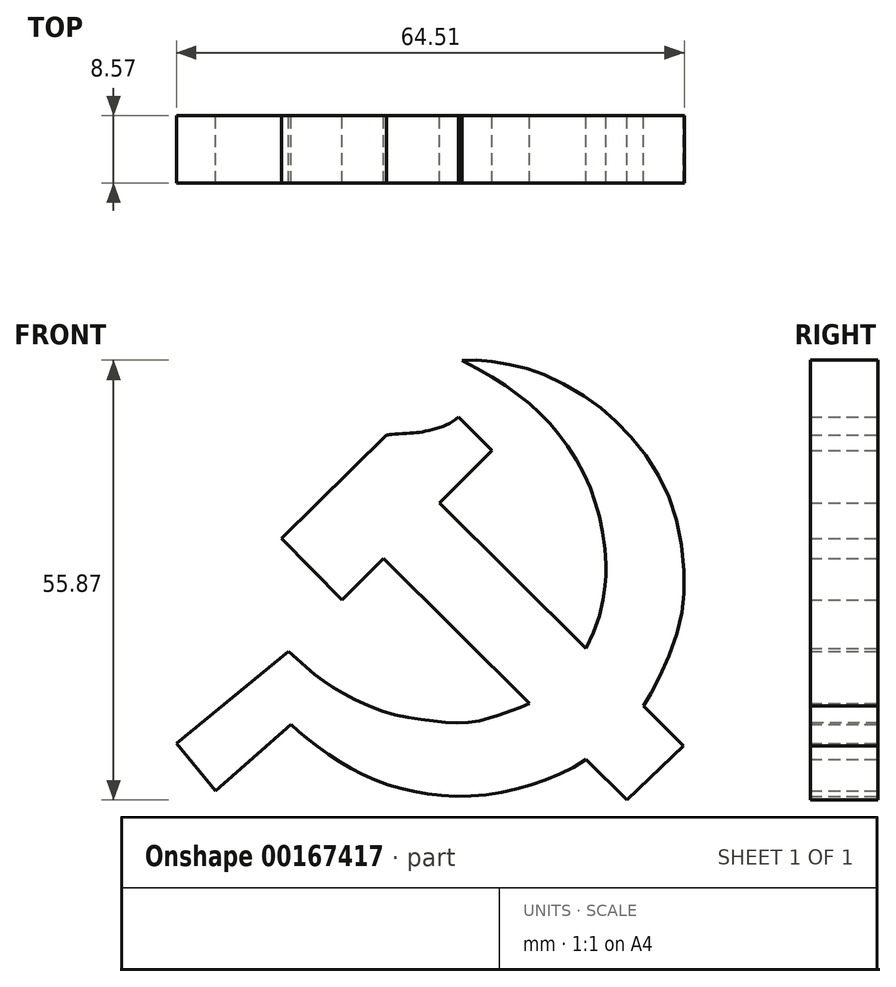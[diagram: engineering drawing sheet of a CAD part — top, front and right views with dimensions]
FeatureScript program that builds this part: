
annotation { "Feature Type Name" : "Feature", "Feature Type Description" : "" }
export const myFeature = defineFeature(function(context is Context, id is Id, definition is map)
    precondition{}
    {
        {
            var Q0;
            Q0=qCreatedBy(makeId("Front.planeOp"),FACE);
            var sketch = newSketch(context, id + "F0", { "sketchPlane" : qUnion([Q0])});
            skLineSegment(sketch, "E0", {"start": v(-17.73, -30.86) * mm, "end": v(-14.06, -35.33) * mm});
            skLineSegment(sketch, "E1", {"start": v(-14.06, -35.33) * mm, "end": v(-6.97, -29.1) * mm});
            skLineSegment(sketch, "E2", {"start": v(-17.73, -30.86) * mm, "end": v(-7.2, -22.22) * mm});
            skFitSpline(sketch, "E3", {"points": [v(-7.2, -22.22) * mm, v(-4.71, -24.37) * mm, v(-2.01, -26.18) * mm, v(2.28, -28.04) * mm, v(6.43, -28.77) * mm, v(9.69, -28.92) * mm, v(12.3, -28.32) * mm, v(13.6, -27.87) * mm, v(15.47, -27.1) * mm, v(18.3, -25.12) * mm, v(20.74, -22.05) * mm, v(22.2, -18.34) * mm, v(22.62, -15.65) * mm, v(22.68, -14.22) * mm, v(22.34, -10.88) * mm, v(21.58, -7.9) * mm, v(20.42, -5.14) * mm, v(18.6, -2.26) * mm, v(16.97, -0.31) * mm, v(14.91, 1.54) * mm, v(12.43, 3.3) * mm, v(9.13, 5.17) * mm], "startDerivative": vector(49.97, -41.74) * mm, "endDerivative": vector(-64.4, 35.2) * mm});
            skFitSpline(sketch, "E4", {"points": [v(9.13, 5.17) * mm, v(10.8, 5.17) * mm, v(12.72, 4.95) * mm, v(15.16, 4.4) * mm, v(17.63, 3.46) * mm, v(21.13, 1.45) * mm, v(23.43, -0.39) * mm, v(26.05, -3.25) * mm, v(28.26, -6.95) * mm, v(29.62, -11.27) * mm, v(30.05, -16.03) * mm, v(29.75, -18.97) * mm, v(28.55, -22.8) * mm, v(27.06, -25.86) * mm, v(26.23, -27.32) * mm, v(23.73, -29.89) * mm, v(20.82, -32.4) * mm, v(17.3, -34.2) * mm, v(13.37, -35.37) * mm, v(9.37, -35.86) * mm, v(5.75, -35.6) * mm, v(2.64, -34.92) * mm, v(-0.37, -33.74) * mm, v(-2.9, -32.25) * mm, v(-5.45, -30.4) * mm, v(-6.97, -29.1) * mm], "startDerivative": vector(57.57, 1.37) * mm, "endDerivative": vector(-44.56, 39.37) * mm});
            skSolve(sketch);
        }
        {
            var Q0;
            Q0=qCreatedBy(makeId("Front.planeOp"),FACE);
            var sketch = newSketch(context, id + "F1", { "sketchPlane" : qUnion([Q0])});
            skLineSegment(sketch, "E5", {"start": v(-7.85, -11.6) * mm, "end": v(2.01, -1.87) * mm});
            skLineSegment(sketch, "E6", {"start": v(-7.85, -11.6) * mm, "end": v(-2.17, -17.36) * mm});
            skLineSegment(sketch, "E7", {"start": v(-2.17, -17.36) * mm, "end": v(1.77, -13.47) * mm});
            skLineSegment(sketch, "E8", {"start": v(1.77, -13.47) * mm, "end": v(24.63, -36.2) * mm});
            skLineSegment(sketch, "E9", {"start": v(24.63, -36.2) * mm, "end": v(30, -31.11) * mm});
            skLineSegment(sketch, "E10", {"start": v(30, -31.11) * mm, "end": v(7.02, -8.28) * mm});
            skLineSegment(sketch, "E11", {"start": v(7.02, -8.28) * mm, "end": v(11.95, -3.31) * mm});
            skLineSegment(sketch, "E12", {"start": v(11.95, -3.31) * mm, "end": v(8.8, -0.18) * mm});
            skFitSpline(sketch, "E13", {"points": [v(8.8, -0.18) * mm, v(7.85, -0.85) * mm, v(6.8, -1.21) * mm, v(5.75, -1.49) * mm, v(4.97, -1.63) * mm, v(4, -1.7) * mm, v(2.8, -1.78) * mm, v(2.3, -1.83) * mm, v(2.01, -1.87) * mm], "startDerivative": vector(-6.33, -5.1) * mm, "endDerivative": vector(-3.87, -0.55) * mm});
            skSolve(sketch);
        }
        {
            var Q0;
            Q0 = qSketchRegion(id + "F1", true);
            extrude(context, id + "F2", {"entities" : qUnion([Q0]), "depth" : 6.35 * mm});
        }
        {
            var Q0;
            Q0 = qSketchRegion(id + "F0", true);
            extrude(context, id + "F3", {"entities" : qUnion([Q0]), "operationType" : NewBodyOperationType.ADD, "depth" : 6.35 * mm});
        }
        {
            var Q0;
            Q0=makeQuery(id+"F2.opExtrude","SWEPT_BODY",BODY,{"disambiguationData":[OSD([sQuery(id+"F1.wireOp",EDGE,"E5"),sQuery(id+"F1.wireOp",EDGE,"E6"),sQuery(id+"F1.wireOp",EDGE,"E7"),sQuery(id+"F1.wireOp",EDGE,"E8"),sQuery(id+"F1.wireOp",EDGE,"E9"),sQuery(id+"F1.wireOp",EDGE,"E10"),sQuery(id+"F1.wireOp",EDGE,"E11"),sQuery(id+"F1.wireOp",EDGE,"E12"),sQuery(id+"F1.wireOp",EDGE,"E13")])]});
            var Q1;
            Q1=makeQuery(id+"F3.opExtrude","SWEPT_BODY",BODY,{"disambiguationData":[OSD([sQuery(id+"F0.wireOp",EDGE,"E0"),sQuery(id+"F0.wireOp",EDGE,"E1"),sQuery(id+"F0.wireOp",EDGE,"E2"),sQuery(id+"F0.wireOp",EDGE,"E3"),sQuery(id+"F0.wireOp",EDGE,"E4")])]});
            var Q2;
            Q2=qCreatedBy(makeId("Origin.pointOp"),VERTEX);
            transform(context, id + "F4", {"entities" : qUnion([Q0, Q1]), "transformType" : TransformType.SCALE_UNIFORMLY, "scale" : 1.35, "scalePoint" : qUnion([Q2]), "makeCopy" : false});
        }
    });
